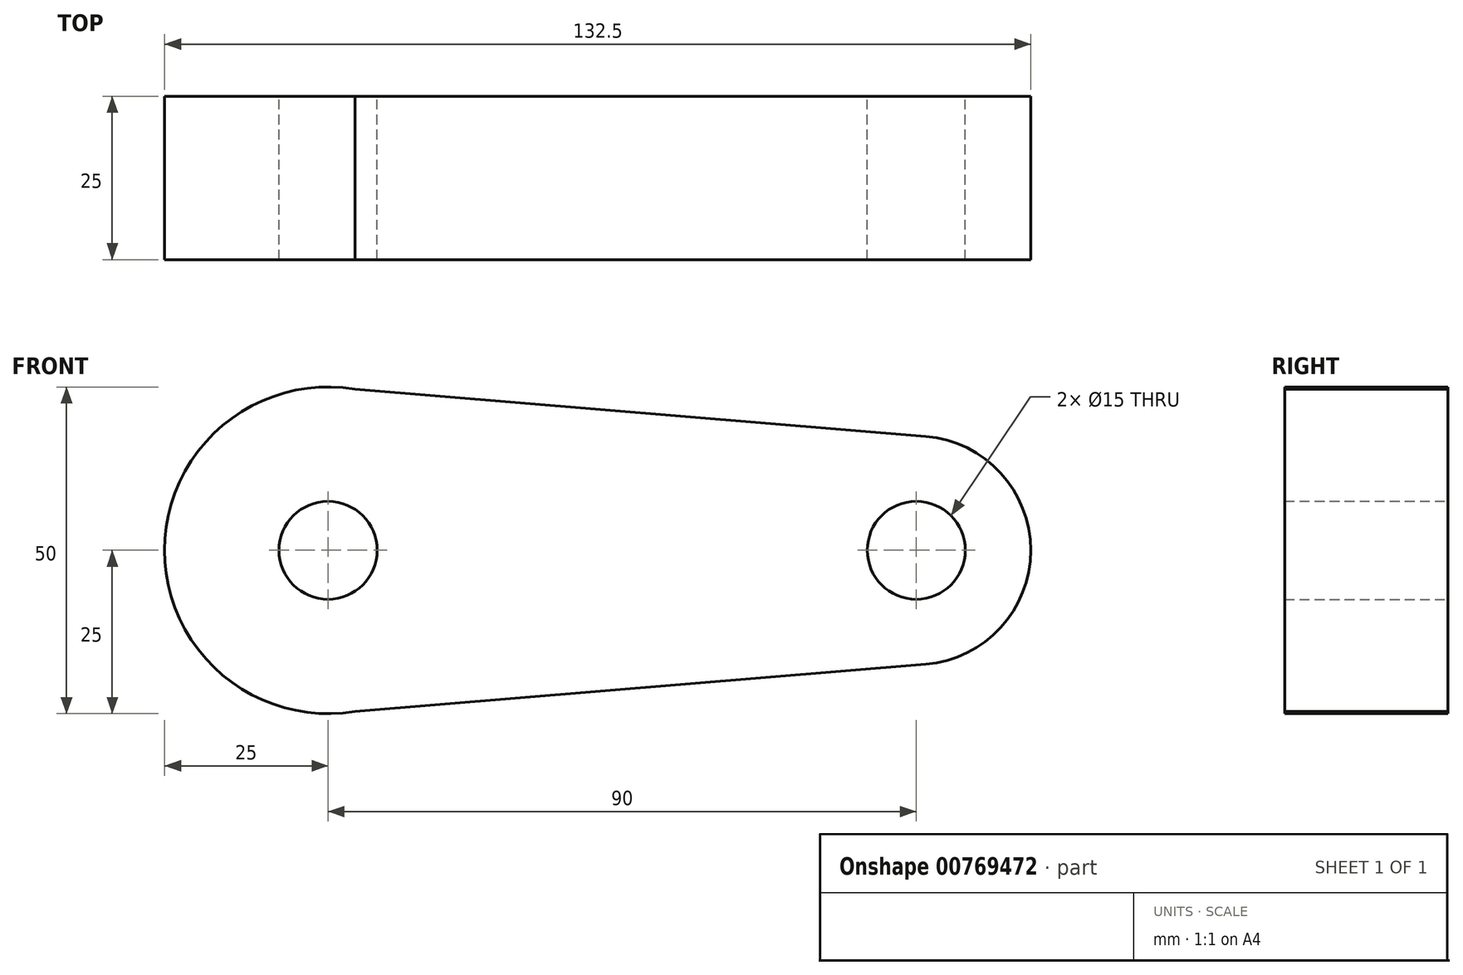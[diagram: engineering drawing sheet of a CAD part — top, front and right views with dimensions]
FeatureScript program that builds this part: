
annotation { "Feature Type Name" : "Feature", "Feature Type Description" : "" }
export const myFeature = defineFeature(function(context is Context, id is Id, definition is map)
    precondition{}
    {
        {
            var Q0;
            Q0=qCreatedBy(makeId("Front.planeOp"),FACE);
            var sketch = newSketch(context, id + "F0", { "sketchPlane" : qUnion([Q0])});
            skCircle(sketch, "E0", {"center": v(0, 0) * mm, "radius": 25 * mm});
            skCircle(sketch, "E1", {"center": v(90, 0) * mm, "radius": 17.5 * mm});
            skLineSegment(sketch, "E2", {"start": v(0, 25) * mm, "end": v(91.44, 17.44) * mm});
            skLineSegment(sketch, "E3", {"start": v(0, -25) * mm, "end": v(91.44, -17.44) * mm});
            skCircle(sketch, "E4", {"center": v(0, 0) * mm, "radius": 7.5 * mm});
            skCircle(sketch, "E5", {"center": v(90, 0) * mm, "radius": 7.5 * mm});
            skSolve(sketch);
        }
        {
            var Q0;
            Q0 = qSketchRegion(id + "F0", true);
            extrude(context, id + "F1", {"entities" : qUnion([Q0]), "depth" : 25 * mm, "offsetDistance" : 25 * mm});
        }
    });
